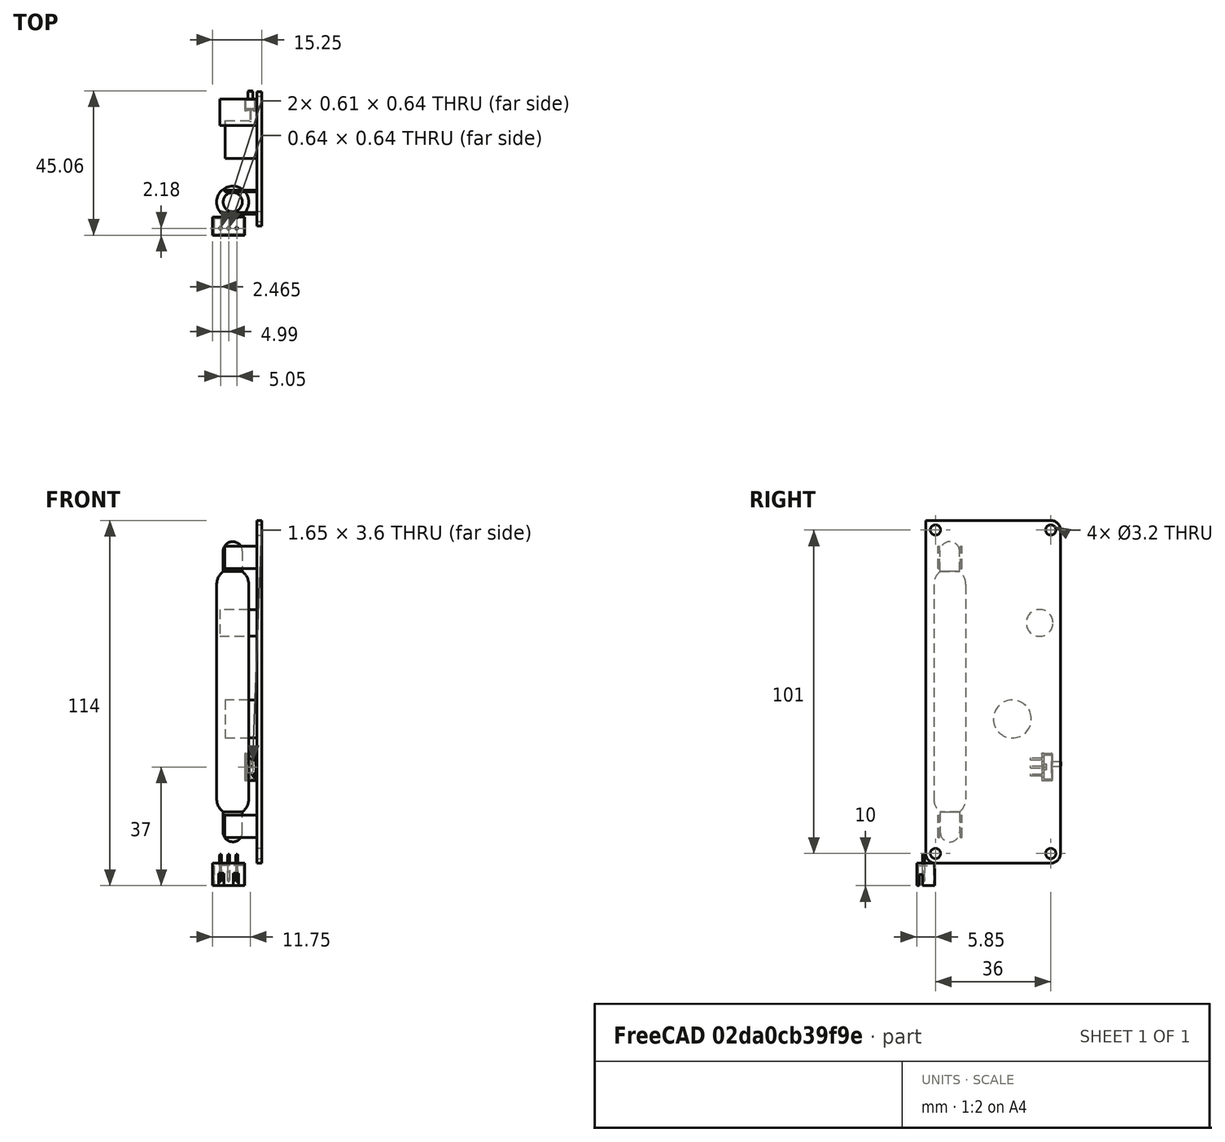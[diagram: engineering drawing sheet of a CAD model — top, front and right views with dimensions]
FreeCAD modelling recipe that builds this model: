
FCSTD DOCUMENT  (FreeCAD 1.0R39109 (Git))
Label: RadiationSensor
License: All rights reserved
LicenseURL: https://en.wikipedia.org/wiki/All_rights_reserved
objects: Part::Cylinder×9, Part::MultiFuse×6, Part::Box×5, Part::Feature×5, Part::Sphere×4, App::Part×3, Part::Cut×1, Part::Fillet×1
note: 31 computed .brp shape members not serialized (recipe doc carries the construction recipe); baked Part::Feature solids carry a one-line shape summary decoded from their .brp

FEATURE [Part::Box] Box  label="PCB"
  AttacherType = Attacher::AttachEngine3D
  Height = 107
  Length = 1.5
  Width = 42
FEATURE [Part::Cylinder] Cylinder  label="Tube"
  Angle = 360
  AttacherType = Attacher::AttachEngine3D
  FirstAngle = 0
  Height = 67
  Placement = pos=(-7.5,7.5,20) rot=(0,0,1;0rad)
  Radius = 5
  SecondAngle = 0
FEATURE [Part::Sphere] Sphere
  Angle1 = -90
  Angle2 = 90
  Angle3 = 180
  AttacherType = Attacher::AttachEngine3D
  Placement = pos=(-7.5,7.5,20) rot=(1,0,0;4.71239rad)
  Radius = 5
FEATURE [Part::Sphere] Sphere001
  Angle1 = -90
  Angle2 = 90
  Angle3 = 180
  AttacherType = Attacher::AttachEngine3D
  Placement = pos=(-7.5,7.5,87) rot=(-1,0,0;4.71239rad)
  Radius = 5
FEATURE [Part::Feature] Part__Feature008  label="switch"
  Placement = pos=(-2,36,30) rot=(-0.57735,0.57735,0.57735;2.0944rad)
  shape: bbox 3.5 x 9.656 x 8.5 mm, 169 faces (baked)
FEATURE [Part::Cylinder] Cylinder001  label="cap1"
  Angle = 360
  AttacherType = Attacher::AttachEngine3D
  FirstAngle = 0
  Height = 9.82
  Placement = pos=(-1.15e-14,27,45) rot=(0,1,0;4.71239rad)
  Radius = 5.93
  SecondAngle = 0
FEATURE [Part::Cylinder] Cylinder002  label="cap2"
  Angle = 360
  AttacherType = Attacher::AttachEngine3D
  FirstAngle = 0
  Height = 11.56
  Placement = pos=(-1.15e-14,35.52,75) rot=(0,1,0;4.71239rad)
  Radius = 4.175
  SecondAngle = 0
FEATURE [Part::Cylinder] Cylinder003  label="Tube001"
  Angle = 360
  AttacherType = Attacher::AttachEngine3D
  FirstAngle = 0
  Height = 6.35
  Placement = pos=(-7.5,7.5,9.65) rot=(0,0,1;0rad)
  Radius = 3
  SecondAngle = 0
FEATURE [Part::Sphere] Sphere002
  Angle1 = -90
  Angle2 = 90
  Angle3 = 180
  AttacherType = Attacher::AttachEngine3D
  Placement = pos=(-7.5,7.5,9.65) rot=(1,0,0;4.71239rad)
  Radius = 3
FEATURE [Part::MultiFuse] Fusion  label="bottomend"
  Refine = true
  Shapes = -> [Cylinder003,Sphere002]
FEATURE [Part::Cylinder] Cylinder004  label="Tube002"
  Angle = 360
  AttacherType = Attacher::AttachEngine3D
  FirstAngle = 0
  Height = 6.35
  Placement = pos=(-7.5,7.5,9.65) rot=(0,0,1;0rad)
  Radius = 3
  SecondAngle = 0
FEATURE [Part::Sphere] Sphere003
  Angle1 = -90
  Angle2 = 90
  Angle3 = 180
  AttacherType = Attacher::AttachEngine3D
  Placement = pos=(-7.5,7.5,9.65) rot=(1,0,0;4.71239rad)
  Radius = 3
FEATURE [Part::MultiFuse] Fusion001  label="topend"
  Placement = pos=(0,15,107) rot=(1,0,0;3.14159rad)
  Refine = true
  Shapes = -> [Cylinder004,Sphere003]
FEATURE [Part::Box] Box001  label="Cube"
  AttacherType = Attacher::AttachEngine3D
  Height = 7
  Length = 10
  Placement = pos=(-10,3.75,8) rot=(0,0,1;0rad)
  Width = 0.5
FEATURE [Part::Box] Box002  label="Cube001"
  AttacherType = Attacher::AttachEngine3D
  Height = 7
  Length = 10
  Placement = pos=(-10,10.75,8) rot=(0,0,1;0rad)
  Width = 0.5
FEATURE [Part::MultiFuse] Fusion002  label="bottom_tubehold"
  Refine = true
  Shapes = -> [Box001,Box002]
FEATURE [Part::Box] Box003  label="Cube002"
  AttacherType = Attacher::AttachEngine3D
  Height = 7
  Length = 10
  Placement = pos=(-10,3.75,92) rot=(0,0,1;0rad)
  Width = 0.5
FEATURE [Part::Box] Box004  label="Cube003"
  AttacherType = Attacher::AttachEngine3D
  Height = 7
  Length = 10
  Placement = pos=(-10,10.75,92) rot=(0,0,1;0rad)
  Width = 0.5
FEATURE [Part::MultiFuse] Fusion003  label="top_tubehold"
  Refine = true
  Shapes = -> [Box003,Box004]
FEATURE [Part::Cylinder] Cylinder005
  Angle = 360
  AttacherType = Attacher::AttachEngine3D
  FirstAngle = 0
  Height = 10
  Placement = pos=(5,3,3) rot=(0,1,0;4.71239rad)
  Radius = 1.6
  SecondAngle = 0
FEATURE [Part::Cylinder] Cylinder006
  Angle = 360
  AttacherType = Attacher::AttachEngine3D
  FirstAngle = 0
  Height = 10
  Placement = pos=(5,39,3) rot=(0,1,0;4.71239rad)
  Radius = 1.6
  SecondAngle = 0
FEATURE [Part::Cylinder] Cylinder007
  Angle = 360
  AttacherType = Attacher::AttachEngine3D
  FirstAngle = 0
  Height = 10
  Placement = pos=(5,3,104) rot=(0,1,0;4.71239rad)
  Radius = 1.6
  SecondAngle = 0
FEATURE [Part::Cylinder] Cylinder008
  Angle = 360
  AttacherType = Attacher::AttachEngine3D
  FirstAngle = 0
  Height = 10
  Placement = pos=(5,39,104) rot=(0,1,0;4.71239rad)
  Radius = 1.6
  SecondAngle = 0
FEATURE [Part::MultiFuse] Fusion004  label="m3_cyl"
  Refine = true
  Shapes = -> [Cylinder005,Cylinder006,Cylinder007,Cylinder008]
FEATURE [Part::Cut] Cut  label="PCB_m3cut"
  Base = -> Box
  Refine = true
  Tool = -> Fusion004
FEATURE [Part::MultiFuse] Fusion005  label="Tube003"
  Refine = true
  Shapes = -> [Cylinder,Sphere,Sphere001,Fusion,Fusion001,Fusion002,Fusion003]
FEATURE [Part::Fillet] Fillet  label="pcb"
  Base = -> Cut
  EdgeLinks = -> Cut [Edge9,Edge12,Edge14]
  Edges = 3 edges r=3: [Edge9,Edge12,Edge14]
FEATURE [Part::Feature] Part__Feature  label="pins"
  Placement = pos=(7.37732,-14.6706,0.356181) rot=(-1,0,0;1.5708rad)
  shape: bbox 0.64 x 0.64 x 8.5 mm, 12 faces (baked)
FEATURE [Part::Feature] Part__Feature001  label="pins001"
  Placement = pos=(7.37732,-14.6706,0.356181) rot=(-1,0,0;1.5708rad)
  shape: bbox 0.64 x 0.64 x 8.5 mm, 12 faces (baked)
FEATURE [Part::Feature] Part__Feature002  label="pins002"
  Placement = pos=(7.37732,-14.6706,0.356181) rot=(-1,0,0;1.5708rad)
  shape: bbox 0.64 x 0.64 x 8.5 mm, 12 faces (baked)
FEATURE [Part::Feature] Part__Feature003  label="SOLID"
  shape: bbox 9.98 x 5.7 x 7 mm, 38 faces (baked)
FEATURE [App::Part] pins  label="pins003"
  Group = -> [Part__Feature,Part__Feature001,Part__Feature002]
  Origin = -> Origin001
FEATURE [App::Part] __pin_RMC_v0  label="3 pin RMC v0"
  Group = -> [pins,Part__Feature003]
  Origin = -> Origin002
  Placement = pos=(-3,12.25,7) rot=(0,0,1;4.71239rad)
FEATURE [App::Part] Part  label="Radiation"
  Group = -> [Part__Feature008,Cylinder001,Cylinder002,Fusion004,Cylinder006,Cylinder007,Cylinder005,Cylinder008,Box,Cut,Sphere001,Sphere002,Cylinder,Fusion001,Fusion,Fusion003,Fusion002,Cylinder004,Cylinder003,Sphere003,Sphere,Box002,Box001,Box004,Box003,Fusion005,Fillet,__pin_RMC_v0]
  Origin = -> Origin
